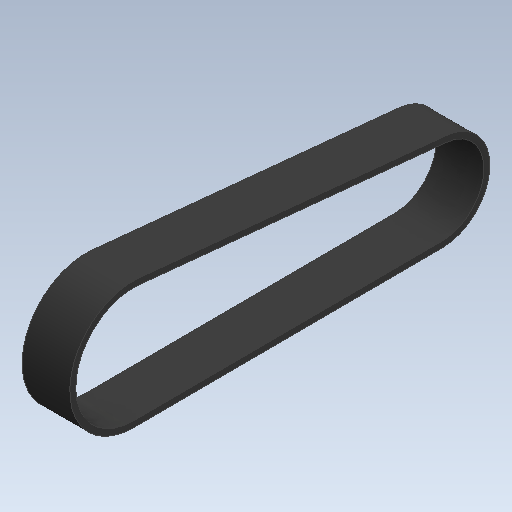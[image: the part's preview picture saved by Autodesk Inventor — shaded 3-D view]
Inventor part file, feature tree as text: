
AUTODESK INVENTOR PART (.ipt)
format: ipt  version: 2020 (Build 240168000, 168)  size: 113,664 bytes
history: native  units: mm
features: other x1, extrude x1, sketch x1
ambient origin geometry x8: Origin, YZ Plane, XZ Plane, XY Plane, X Axis, Y Axis, Z Axis, Center Point
bodies: Body1 (feature_tree)
feature tree (3):
  other  "Твердое тело1"
  extrude  "Выдавливание1"  Depth=38.872mm
  sketch  "Эскиз1"
